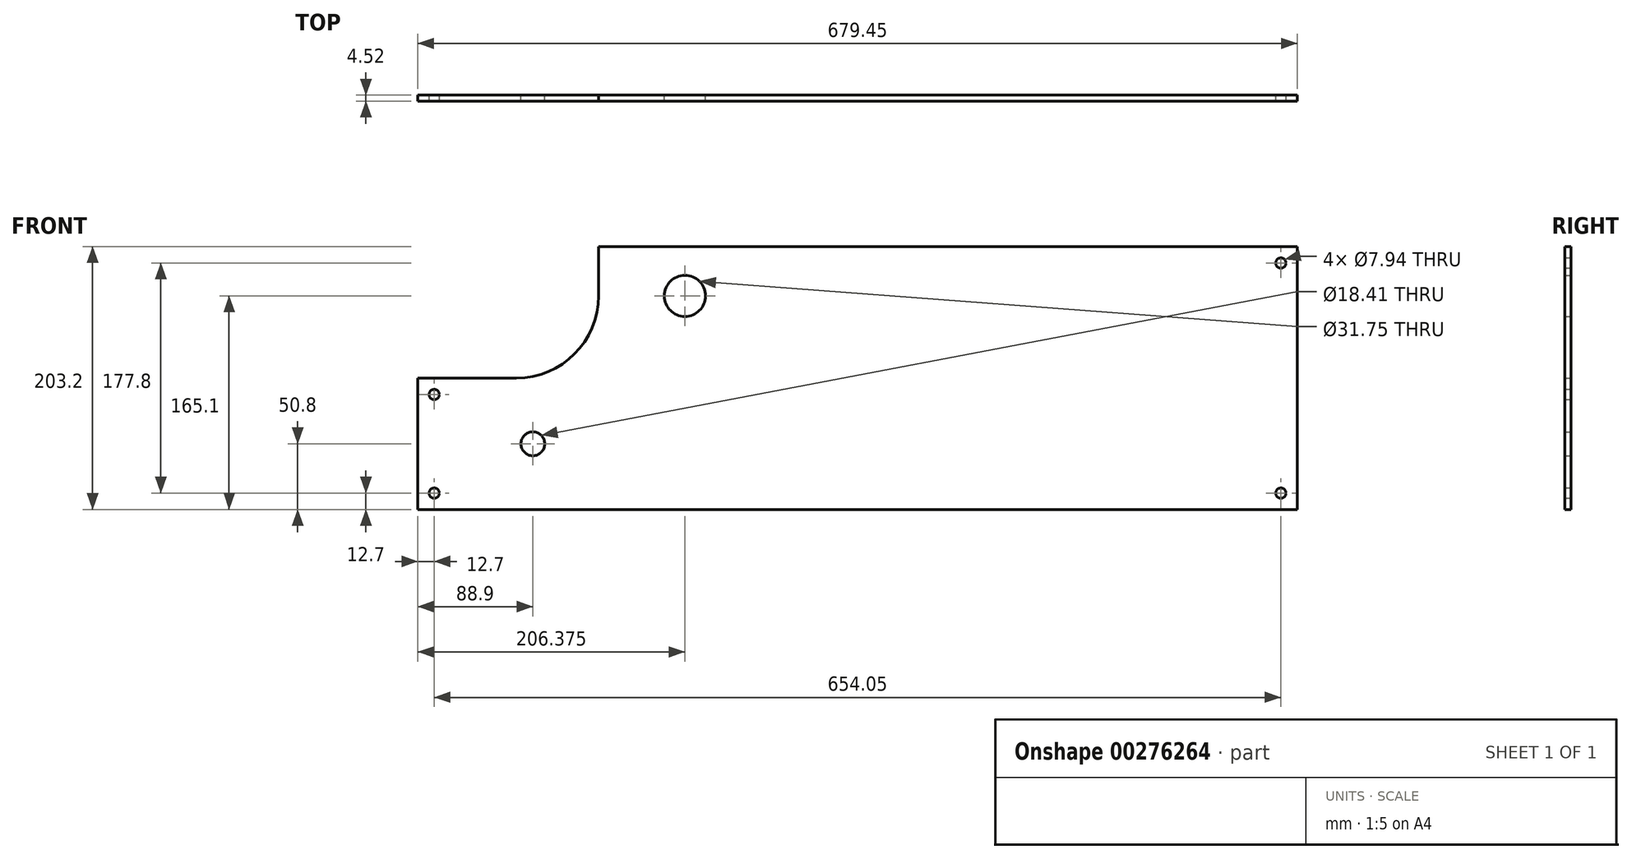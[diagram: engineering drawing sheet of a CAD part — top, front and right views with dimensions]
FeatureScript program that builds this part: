
annotation { "Feature Type Name" : "Feature", "Feature Type Description" : "" }
export const myFeature = defineFeature(function(context is Context, id is Id, definition is map)
    precondition{}
    {
        {
            var Q0;
            Q0=qCreatedBy(makeId("Front.planeOp"),FACE);
            var sketch = newSketch(context, id + "F0", { "sketchPlane" : qUnion([Q0])});
            skLineSegment(sketch, "E0", {"start": v(0, 0) * mm, "end": v(-679.45, 0) * mm});
            skLineSegment(sketch, "E1", {"start": v(0, 0) * mm, "end": v(0, 203.2) * mm});
            skLineSegment(sketch, "E2", {"start": v(0, 203.2) * mm, "end": v(-539.75, 203.2) * mm});
            skLineSegment(sketch, "E3", {"start": v(-679.45, 0) * mm, "end": v(-679.45, 101.6) * mm});
            skLineSegment(sketch, "E4", {"start": v(-679.45, 101.6) * mm, "end": v(-603.25, 101.6) * mm});
            skLineSegment(sketch, "E5", {"start": v(-539.75, 203.2) * mm, "end": v(-539.75, 165.1) * mm});
            skPoint(sketch, "E6.visualSharp", {"position": v(-539.75, 101.6) * mm});
            skArc(sketch, "E6.filletArc", {"start": v(-603.25, 101.6) * mm, "mid": v(-558.35, 120.2) * mm, "end": v(-539.75, 165.1) * mm});
            skCircle(sketch, "E7", {"center": v(-473.08, 165.1) * mm, "radius": 15.88 * mm});
            skCircle(sketch, "E8", {"center": v(-590.55, 50.8) * mm, "radius": 9.2 * mm});
            skCircle(sketch, "E9", {"center": v(-666.75, 12.7) * mm, "radius": 3.97 * mm});
            skCircle(sketch, "E10", {"center": v(-666.75, 88.9) * mm, "radius": 3.97 * mm});
            skCircle(sketch, "E11", {"center": v(-12.7, 190.5) * mm, "radius": 3.97 * mm});
            skCircle(sketch, "E12", {"center": v(-12.7, 12.7) * mm, "radius": 3.97 * mm});
            skSolve(sketch);
        }
        {
            var Q0;
            Q0 = qSketchRegion(id + "F0", true);
            extrude(context, id + "F1", {"entities" : qUnion([Q0]), "depth" : 4.52 * mm});
        }
    });
